# Revit family: Platek_Circus
name_source: partatom
category: Apparecchi per illuminazione
revit_build: Autodesk Revit 2017 (Build: 20160225_1515(x64)
units: mm (PartAtom-declared; Revit-internal decimal feet)

## family parameters
Basato su piano di lavoro = Sì
Condiviso = No
Punto di calcolo locali = No
Quota connettore circolare = Usa diametro
Sempre verticale = No
Sorgente d'illuminazione = Sì
Taglio con vuoti quando caricato = No
Tipo di parte = Normale

## types (2) — shared parameters
Angolo inclinazione = 90.00°
CRI = >80
Cable Lenght = Cable input Ø 1÷18 mm
Carico apparente = 0 VA
Colour Temperature = 3000 K
Commenti sul tipo = Ceiling, Balconies, Front Porch
Descrizione = Outdoor lighting, Downlight, Ceiling mounted
Diffuse Type = Diffuse Glass
Dimmable = No
Emetti da diametro cerchio = 144 mm  [stored 0.472441 ft]
Energy Efficiency Rating = A/A+/A++
Filtro dei colori = 16777215
Frequency = 50/60 Hz
IK Rating = IK08
IP Rating = IP65
Immagine tipo = circus_plafoniera.jpg
Insulation Class = 1
L.260_400 = Sì
LED Protection = Surge protection included
Lampada = LED
Light Source = PLK_Light Source
Manufacturer Comment = IP68 Connector Included
Modello = Circus Downlight
Mounting Type = Ceiling
Nota chiave = 5mm flat tempered sandblasted glass; Other Led colors available on request
Power Supply Unit = Included
Product Dimension = L114mm x D210mm
Product Documentation Link = http://www.platek.eu
Product Page URL = http://www.platek.eu
Produttore = PLATEK SRL
Prospetto di default = 1219 mm
Rendi la forma visibile nel rendering = No
Supply Voltage = 230 V
Supply Voltage Max = 240 V
Supply Voltage Min = 220 V
URL = www.platek.eu
Variazione temperatura colore lampada con luminosità attenuata = <Nessuno>

## per-type parameters (varying)
| type | Body | Codice assieme | File diagramma fotometrico | Luminaire Luminous Flux | Luminaire Luminous Intensity | Luminaire Wattage | PLATEK Article Code |
| 4520518_18,5W_LED_3000K_Downlight | PLK_06_Grey | 4520518.01(Black); 4520518.02(White); 4520518.07(Corten); 4520518.09(Bronze) | 4520518.IES | 1850 lm | 1057 cd | 19 W | 4520518 |
| 4520318_14W_LED_3000K_Downlight | PLK_Grey | 4520318.01(Black); 4520318.02(White); 4520318.07(Corten); 4520318.09(Bronze) | 4520318.IES | 1740 lm | 995 cd | 14 W | 4520318 |

note: [stored X ft] marks values corroborated as IEEE doubles in the binary element streams (Revit-internal decimal feet)
